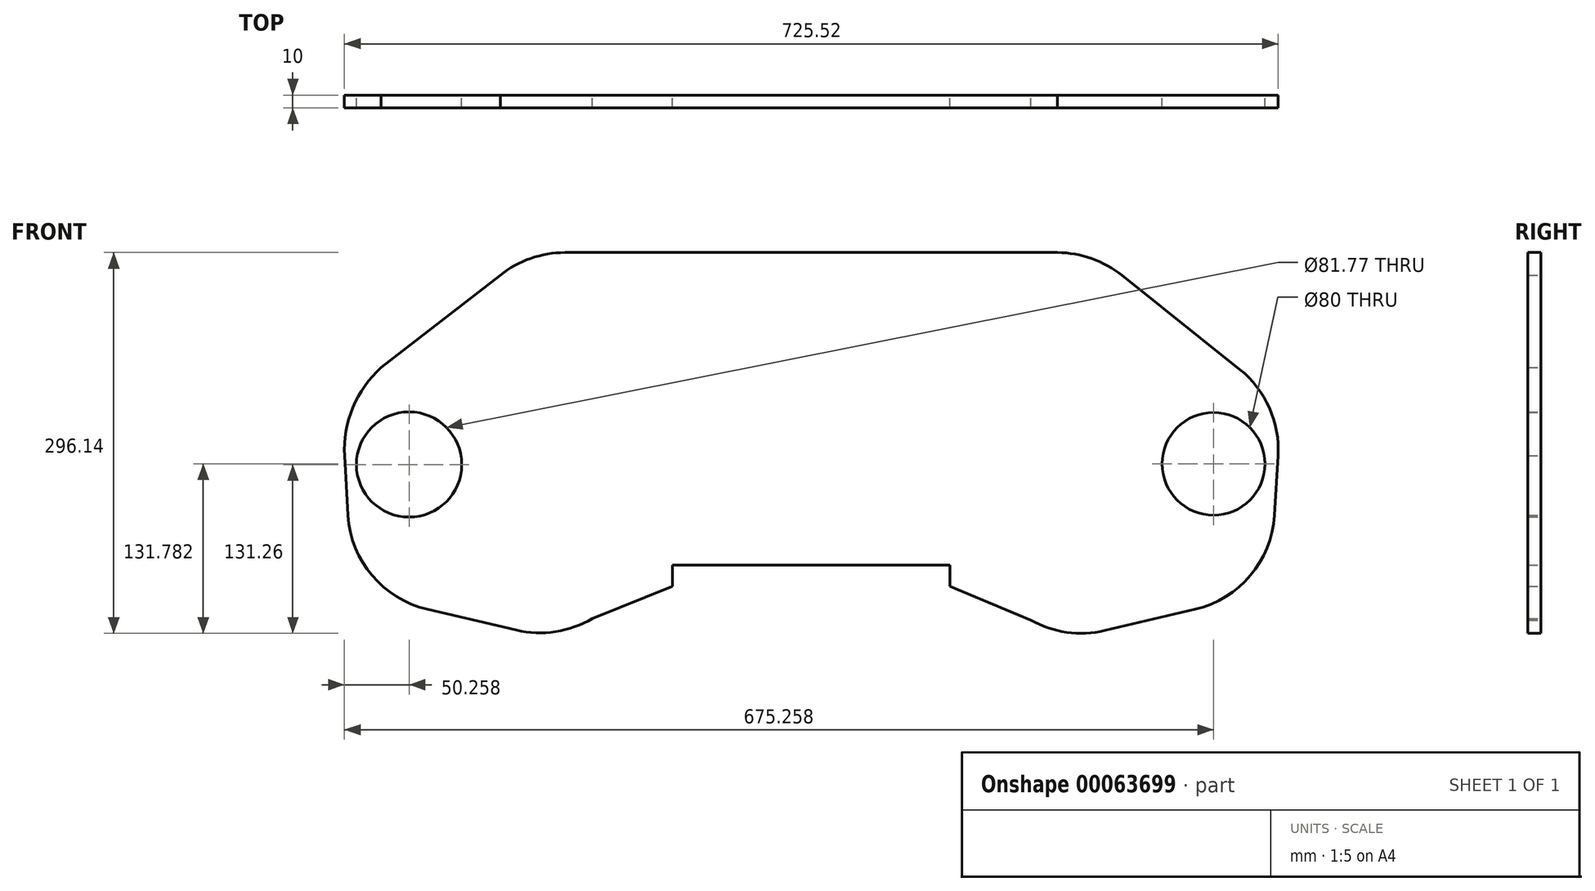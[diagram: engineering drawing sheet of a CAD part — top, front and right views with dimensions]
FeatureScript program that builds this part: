
annotation { "Feature Type Name" : "Feature", "Feature Type Description" : "" }
export const myFeature = defineFeature(function(context is Context, id is Id, definition is map)
    precondition{}
    {
        {
            var Q0;
            Q0=qCreatedBy(makeId("Front.planeOp"),FACE);
            var sketch = newSketch(context, id + "F0", { "sketchPlane" : qUnion([Q0])});
            skLineSegment(sketch, "E0", {"start": v(107.78, -86.22) * mm, "end": v(107.78, -69.71) * mm});
            skLineSegment(sketch, "E1", {"start": v(107.78, -69.71) * mm, "end": v(-107.78, -69.71) * mm});
            skArc(sketch, "E2", {"start": v(-359.86, -30.91) * mm, "mid": v(-341.19, -77.66) * mm, "end": v(-298.29, -104) * mm});
            skArc(sketch, "E3", {"start": v(-334.1, 84.04) * mm, "mid": v(-356.08, 52.96) * mm, "end": v(-362.64, 15.45) * mm});
            skArc(sketch, "E4", {"start": v(-191.47, 173.48) * mm, "mid": v(-218, 168.96) * mm, "end": v(-241.52, 155.9) * mm});
            skArc(sketch, "E5", {"start": v(241.43, 155.72) * mm, "mid": v(217.88, 168.8) * mm, "end": v(191.37, 173.53) * mm});
            skArc(sketch, "E6", {"start": v(362.64, 15.45) * mm, "mid": v(355.92, 52.67) * mm, "end": v(332.84, 82.65) * mm});
            skArc(sketch, "E7", {"start": v(298.29, -104) * mm, "mid": v(341.19, -77.66) * mm, "end": v(359.86, -30.91) * mm});
            skArc(sketch, "E8", {"start": v(170.5, -112.31) * mm, "mid": v(198.5, -121.81) * mm, "end": v(228.04, -120.49) * mm});
            skArc(sketch, "E9", {"start": v(-229.28, -120.2) * mm, "mid": v(-198.76, -121.37) * mm, "end": v(-170.01, -111.02) * mm});
            skLineSegment(sketch, "E10", {"start": v(-107.78, -86.22) * mm, "end": v(-107.78, -69.71) * mm});
            skCircle(sketch, "E11", {"center": v(-312.48, 8.65) * mm, "radius": 25 * mm});
            skCircle(sketch, "E12", {"center": v(312.52, 9.17) * mm, "radius": 22.72 * mm});
            skLineSegment(sketch, "E13", {"start": v(-191.47, 173.48) * mm, "end": v(191.37, 173.53) * mm});
            skCircle(sketch, "E14", {"center": v(-312.48, 8.65) * mm, "radius": 40.89 * mm});
            skCircle(sketch, "E15", {"center": v(312.52, 9.17) * mm, "radius": 40 * mm});
            skLineSegment(sketch, "E16", {"start": v(-241.52, 155.9) * mm, "end": v(-334.1, 84.04) * mm});
            skLineSegment(sketch, "E17", {"start": v(-362.64, 15.45) * mm, "end": v(-359.86, -30.91) * mm});
            skLineSegment(sketch, "E18", {"start": v(-298.29, -104) * mm, "end": v(-229.28, -120.2) * mm});
            skLineSegment(sketch, "E19", {"start": v(107.78, -86.22) * mm, "end": v(170.5, -112.31) * mm});
            skLineSegment(sketch, "E20", {"start": v(228.04, -120.49) * mm, "end": v(298.29, -104) * mm});
            skLineSegment(sketch, "E21", {"start": v(359.86, -30.91) * mm, "end": v(362.64, 15.45) * mm});
            skLineSegment(sketch, "E22", {"start": v(332.84, 82.65) * mm, "end": v(241.43, 155.72) * mm});
            skLineSegment(sketch, "E23", {"start": v(-107.78, -86.22) * mm, "end": v(-170.01, -111.02) * mm});
            skSolve(sketch);
        }
        {
            var Q0;
            Q0=makeQuery(id+"F0.imprint","IMPRINT",FACE,{"disambiguationData":[TD([[makeQuery(id+"F0.imprint","IMPRINT",EDGE,{"derivedFrom":sQuery(id+"F0.wireOp",EDGE,"E3")}),1.0]])]});
            extrude(context, id + "F1", {"entities" : qUnion([Q0]), "depth" : 10 * mm});
        }
    });
